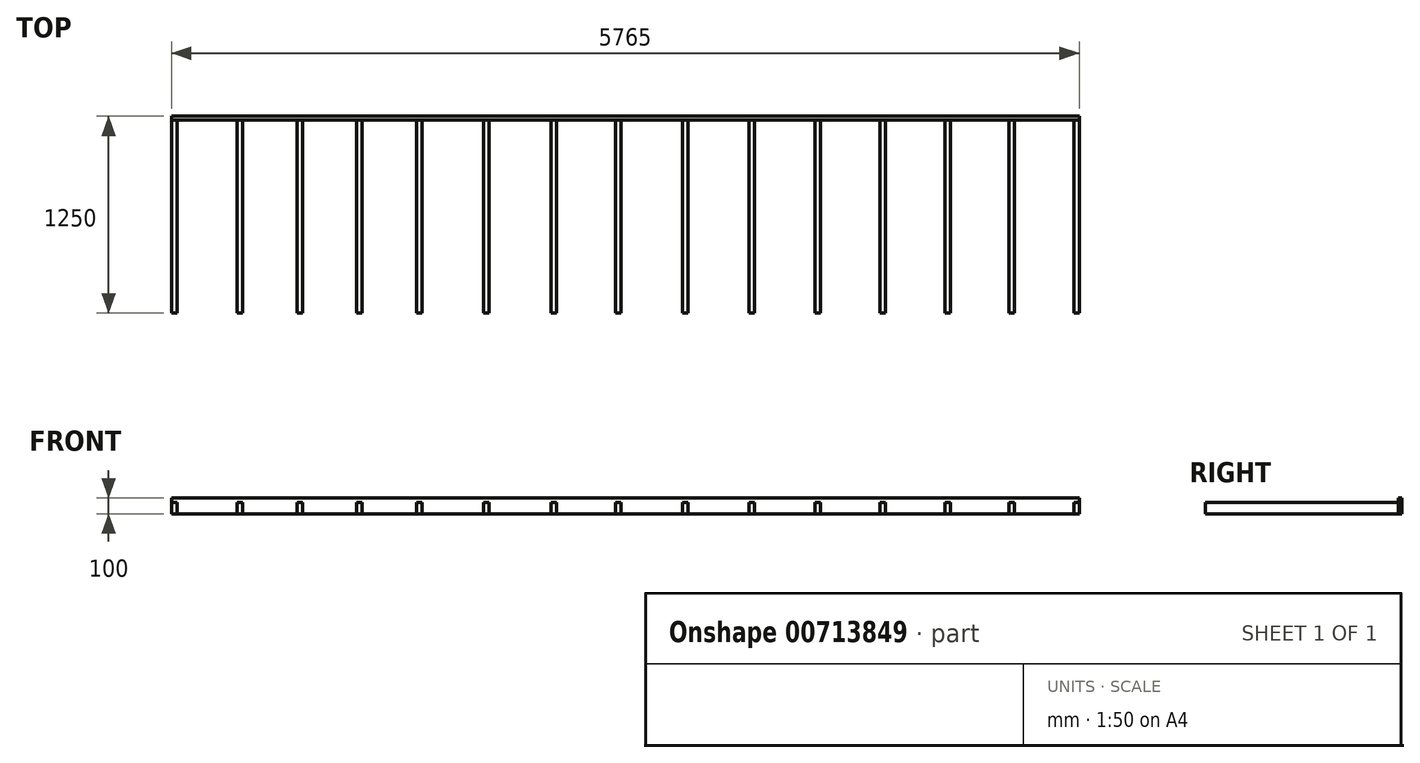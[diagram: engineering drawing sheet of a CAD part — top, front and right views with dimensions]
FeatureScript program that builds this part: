
annotation { "Feature Type Name" : "Feature", "Feature Type Description" : "" }
export const myFeature = defineFeature(function(context is Context, id is Id, definition is map)
    precondition{}
    {
        {
            var Q0;
            Q0=qCreatedBy(makeId("Top.planeOp"),FACE);
            var sketch = newSketch(context, id + "F0", { "sketchPlane" : qUnion([Q0])});
            skLineSegment(sketch, "E0", {"start": v(0, 0) * mm, "end": v(35, 0) * mm});
            skLineSegment(sketch, "E1.1.0.0", {"start": v(415, 0) * mm, "end": v(450, 0) * mm});
            skLineSegment(sketch, "E1.2.0.0", {"start": v(796, 0) * mm, "end": v(831, 0) * mm});
            skLineSegment(sketch, "E1.3.0.0", {"start": v(1176, 0) * mm, "end": v(1211, 0) * mm});
            skLineSegment(sketch, "E1.4.0.0", {"start": v(1556, 0) * mm, "end": v(1591, 0) * mm});
            skLineSegment(sketch, "E1.5.0.0", {"start": v(1981, 0) * mm, "end": v(2016, 0) * mm});
            skLineSegment(sketch, "E1.6.0.0", {"start": v(2410, 0) * mm, "end": v(2445, 0) * mm});
            skLineSegment(sketch, "E1.7.0.0", {"start": v(2821, 0) * mm, "end": v(2856, 0) * mm});
            skLineSegment(sketch, "E1.8.0.0", {"start": v(3244, 0) * mm, "end": v(3279, 0) * mm});
            skLineSegment(sketch, "E1.9.0.0", {"start": v(3666, 0) * mm, "end": v(3701, 0) * mm});
            skLineSegment(sketch, "E1.10.0.0", {"start": v(4087, 0) * mm, "end": v(4122, 0) * mm});
            skLineSegment(sketch, "E1.11.0.0", {"start": v(4498, 0) * mm, "end": v(4533, 0) * mm});
            skLineSegment(sketch, "E1.12.0.0", {"start": v(4912, 0) * mm, "end": v(4947, 0) * mm});
            skLineSegment(sketch, "E1.13.0.0", {"start": v(5319, 0) * mm, "end": v(5354, 0) * mm});
            skLineSegment(sketch, "E1.14.0.0", {"start": v(5730, 0) * mm, "end": v(5765, 0) * mm});
            skLineSegment(sketch, "E2.top", {"start": v(0, 1227) * mm, "end": v(35, 1227) * mm});
            skLineSegment(sketch, "E2.left", {"start": v(0, 0) * mm, "end": v(0, 1227) * mm});
            skLineSegment(sketch, "E2.right", {"start": v(35, 0) * mm, "end": v(35, 1227) * mm});
            skLineSegment(sketch, "E3.top", {"start": v(415, 1227) * mm, "end": v(450, 1227) * mm});
            skLineSegment(sketch, "E3.left", {"start": v(415, 0) * mm, "end": v(415, 1227) * mm});
            skLineSegment(sketch, "E3.right", {"start": v(450, 0) * mm, "end": v(450, 1227) * mm});
            skLineSegment(sketch, "E4.top", {"start": v(796, 1227) * mm, "end": v(831, 1227) * mm});
            skLineSegment(sketch, "E4.left", {"start": v(796, 0) * mm, "end": v(796, 1227) * mm});
            skLineSegment(sketch, "E4.right", {"start": v(831, 0) * mm, "end": v(831, 1227) * mm});
            skLineSegment(sketch, "E5.top", {"start": v(1176, 1227) * mm, "end": v(1211, 1227) * mm});
            skLineSegment(sketch, "E5.left", {"start": v(1176, 0) * mm, "end": v(1176, 1227) * mm});
            skLineSegment(sketch, "E5.right", {"start": v(1211, 0) * mm, "end": v(1211, 1227) * mm});
            skLineSegment(sketch, "E6.top", {"start": v(1556, 1227) * mm, "end": v(1591, 1227) * mm});
            skLineSegment(sketch, "E6.left", {"start": v(1556, 0) * mm, "end": v(1556, 1227) * mm});
            skLineSegment(sketch, "E6.right", {"start": v(1591, 0) * mm, "end": v(1591, 1227) * mm});
            skLineSegment(sketch, "E7.top", {"start": v(1981, 1227) * mm, "end": v(2016, 1227) * mm});
            skLineSegment(sketch, "E7.left", {"start": v(1981, 0) * mm, "end": v(1981, 1227) * mm});
            skLineSegment(sketch, "E7.right", {"start": v(2016, 0) * mm, "end": v(2016, 1227) * mm});
            skLineSegment(sketch, "E8.top", {"start": v(2410, 1227) * mm, "end": v(2445, 1227) * mm});
            skLineSegment(sketch, "E8.left", {"start": v(2410, 0) * mm, "end": v(2410, 1227) * mm});
            skLineSegment(sketch, "E8.right", {"start": v(2445, 0) * mm, "end": v(2445, 1227) * mm});
            skLineSegment(sketch, "E9.top", {"start": v(2821, 1227) * mm, "end": v(2856, 1227) * mm});
            skLineSegment(sketch, "E9.left", {"start": v(2821, 0) * mm, "end": v(2821, 1227) * mm});
            skLineSegment(sketch, "E9.right", {"start": v(2856, 0) * mm, "end": v(2856, 1227) * mm});
            skLineSegment(sketch, "E10.top", {"start": v(3244, 1227) * mm, "end": v(3279, 1227) * mm});
            skLineSegment(sketch, "E10.left", {"start": v(3244, 0) * mm, "end": v(3244, 1227) * mm});
            skLineSegment(sketch, "E10.right", {"start": v(3279, 0) * mm, "end": v(3279, 1227) * mm});
            skLineSegment(sketch, "E11.top", {"start": v(3666, 1227) * mm, "end": v(3701, 1227) * mm});
            skLineSegment(sketch, "E11.left", {"start": v(3666, 0) * mm, "end": v(3666, 1227) * mm});
            skLineSegment(sketch, "E11.right", {"start": v(3701, 0) * mm, "end": v(3701, 1227) * mm});
            skLineSegment(sketch, "E12.top", {"start": v(4087, 1227) * mm, "end": v(4122, 1227) * mm});
            skLineSegment(sketch, "E12.left", {"start": v(4087, 0) * mm, "end": v(4087, 1227) * mm});
            skLineSegment(sketch, "E12.right", {"start": v(4122, 0) * mm, "end": v(4122, 1227) * mm});
            skLineSegment(sketch, "E13.top", {"start": v(4498, 1227) * mm, "end": v(4533, 1227) * mm});
            skLineSegment(sketch, "E13.left", {"start": v(4498, 0) * mm, "end": v(4498, 1227) * mm});
            skLineSegment(sketch, "E13.right", {"start": v(4533, 0) * mm, "end": v(4533, 1227) * mm});
            skLineSegment(sketch, "E14.top", {"start": v(4912, 1227) * mm, "end": v(4947, 1227) * mm});
            skLineSegment(sketch, "E14.left", {"start": v(4912, 0) * mm, "end": v(4912, 1227) * mm});
            skLineSegment(sketch, "E14.right", {"start": v(4947, 0) * mm, "end": v(4947, 1227) * mm});
            skLineSegment(sketch, "E15.top", {"start": v(5319, 1227) * mm, "end": v(5354, 1227) * mm});
            skLineSegment(sketch, "E15.left", {"start": v(5319, 0) * mm, "end": v(5319, 1227) * mm});
            skLineSegment(sketch, "E15.right", {"start": v(5354, 0) * mm, "end": v(5354, 1227) * mm});
            skLineSegment(sketch, "E16.top", {"start": v(5730, 1227) * mm, "end": v(5765, 1227) * mm});
            skLineSegment(sketch, "E16.left", {"start": v(5730, 0) * mm, "end": v(5730, 1227) * mm});
            skLineSegment(sketch, "E16.right", {"start": v(5765, 0) * mm, "end": v(5765, 1227) * mm});
            skLineSegment(sketch, "E17.left", {"start": v(0, 1227) * mm, "end": v(0, 1250) * mm});
            skLineSegment(sketch, "E18", {"start": v(0, 0) * mm, "end": v(5765, 0) * mm});
            skLineSegment(sketch, "E19.bottom", {"start": v(5765, 1227) * mm, "end": v(0, 1227) * mm});
            skLineSegment(sketch, "E19.top", {"start": v(5765, 1250) * mm, "end": v(0, 1250) * mm});
            skLineSegment(sketch, "E19.left", {"start": v(5765, 1227) * mm, "end": v(5765, 1250) * mm});
            skSolve(sketch);
        }
        {
            var Q0;
            {var subQ0=sQuery(id+"F0.wireOp",EDGE,"E2.left");Q0=makeQuery(id+"F0.imprint","IMPRINT",FACE,{"disambiguationData":[TD([[makeQuery(id+"F0.imprint","IMPRINT",EDGE,{"derivedFrom":subQ0}),-1.0]])]});}
            var Q1;
            {var subQ0=sQuery(id+"F0.wireOp",EDGE,"E3.left");Q1=makeQuery(id+"F0.imprint","IMPRINT",FACE,{"disambiguationData":[TD([[makeQuery(id+"F0.imprint","IMPRINT",EDGE,{"derivedFrom":subQ0}),-1.0]])]});}
            var Q2;
            {var subQ0=sQuery(id+"F0.wireOp",EDGE,"E4.left");Q2=makeQuery(id+"F0.imprint","IMPRINT",FACE,{"disambiguationData":[TD([[makeQuery(id+"F0.imprint","IMPRINT",EDGE,{"derivedFrom":subQ0}),-1.0]])]});}
            var Q3;
            {var subQ0=sQuery(id+"F0.wireOp",EDGE,"E5.left");Q3=makeQuery(id+"F0.imprint","IMPRINT",FACE,{"disambiguationData":[TD([[makeQuery(id+"F0.imprint","IMPRINT",EDGE,{"derivedFrom":subQ0}),-1.0]])]});}
            var Q4;
            {var subQ0=sQuery(id+"F0.wireOp",EDGE,"E6.left");Q4=makeQuery(id+"F0.imprint","IMPRINT",FACE,{"disambiguationData":[TD([[makeQuery(id+"F0.imprint","IMPRINT",EDGE,{"derivedFrom":subQ0}),-1.0]])]});}
            var Q5;
            {var subQ0=sQuery(id+"F0.wireOp",EDGE,"E7.left");Q5=makeQuery(id+"F0.imprint","IMPRINT",FACE,{"disambiguationData":[TD([[makeQuery(id+"F0.imprint","IMPRINT",EDGE,{"derivedFrom":subQ0}),-1.0]])]});}
            var Q6;
            {var subQ0=sQuery(id+"F0.wireOp",EDGE,"E8.left");Q6=makeQuery(id+"F0.imprint","IMPRINT",FACE,{"disambiguationData":[TD([[makeQuery(id+"F0.imprint","IMPRINT",EDGE,{"derivedFrom":subQ0}),-1.0]])]});}
            var Q7;
            {var subQ0=sQuery(id+"F0.wireOp",EDGE,"E9.left");Q7=makeQuery(id+"F0.imprint","IMPRINT",FACE,{"disambiguationData":[TD([[makeQuery(id+"F0.imprint","IMPRINT",EDGE,{"derivedFrom":subQ0}),-1.0]])]});}
            var Q8;
            {var subQ0=sQuery(id+"F0.wireOp",EDGE,"E10.left");Q8=makeQuery(id+"F0.imprint","IMPRINT",FACE,{"disambiguationData":[TD([[makeQuery(id+"F0.imprint","IMPRINT",EDGE,{"derivedFrom":subQ0}),-1.0]])]});}
            var Q9;
            {var subQ0=sQuery(id+"F0.wireOp",EDGE,"E11.left");Q9=makeQuery(id+"F0.imprint","IMPRINT",FACE,{"disambiguationData":[TD([[makeQuery(id+"F0.imprint","IMPRINT",EDGE,{"derivedFrom":subQ0}),-1.0]])]});}
            var Q10;
            {var subQ0=sQuery(id+"F0.wireOp",EDGE,"E12.left");Q10=makeQuery(id+"F0.imprint","IMPRINT",FACE,{"disambiguationData":[TD([[makeQuery(id+"F0.imprint","IMPRINT",EDGE,{"derivedFrom":subQ0}),-1.0]])]});}
            var Q11;
            {var subQ0=sQuery(id+"F0.wireOp",EDGE,"E13.left");Q11=makeQuery(id+"F0.imprint","IMPRINT",FACE,{"disambiguationData":[TD([[makeQuery(id+"F0.imprint","IMPRINT",EDGE,{"derivedFrom":subQ0}),-1.0]])]});}
            var Q12;
            {var subQ0=sQuery(id+"F0.wireOp",EDGE,"E14.left");Q12=makeQuery(id+"F0.imprint","IMPRINT",FACE,{"disambiguationData":[TD([[makeQuery(id+"F0.imprint","IMPRINT",EDGE,{"derivedFrom":subQ0}),-1.0]])]});}
            var Q13;
            {var subQ0=sQuery(id+"F0.wireOp",EDGE,"E15.left");Q13=makeQuery(id+"F0.imprint","IMPRINT",FACE,{"disambiguationData":[TD([[makeQuery(id+"F0.imprint","IMPRINT",EDGE,{"derivedFrom":subQ0}),-1.0]])]});}
            var Q14;
            {var subQ0=sQuery(id+"F0.wireOp",EDGE,"E16.left");Q14=makeQuery(id+"F0.imprint","IMPRINT",FACE,{"disambiguationData":[TD([[makeQuery(id+"F0.imprint","IMPRINT",EDGE,{"derivedFrom":subQ0}),-1.0]])]});}
            extrude(context, id + "F1", {"entities" : qUnion([Q0, Q1, Q2, Q3, Q4, Q5, Q6, Q7, Q8, Q9, Q10, Q11, Q12, Q13, Q14]), "depth" : 73 * mm, "offsetDistance" : 25 * mm});
        }
        {
            var Q0;
            Q0=makeQuery(id+"F0.imprint","IMPRINT",FACE,{"disambiguationData":[TD([[makeQuery(id+"F0.imprint","IMPRINT",EDGE,{"derivedFrom":sQuery(id+"F0.wireOp",EDGE,"E19.top")}),1.0]])]});
            extrude(context, id + "F2", {"entities" : qUnion([Q0]), "depth" : 100 * mm, "offsetDistance" : 25 * mm});
        }
    });
